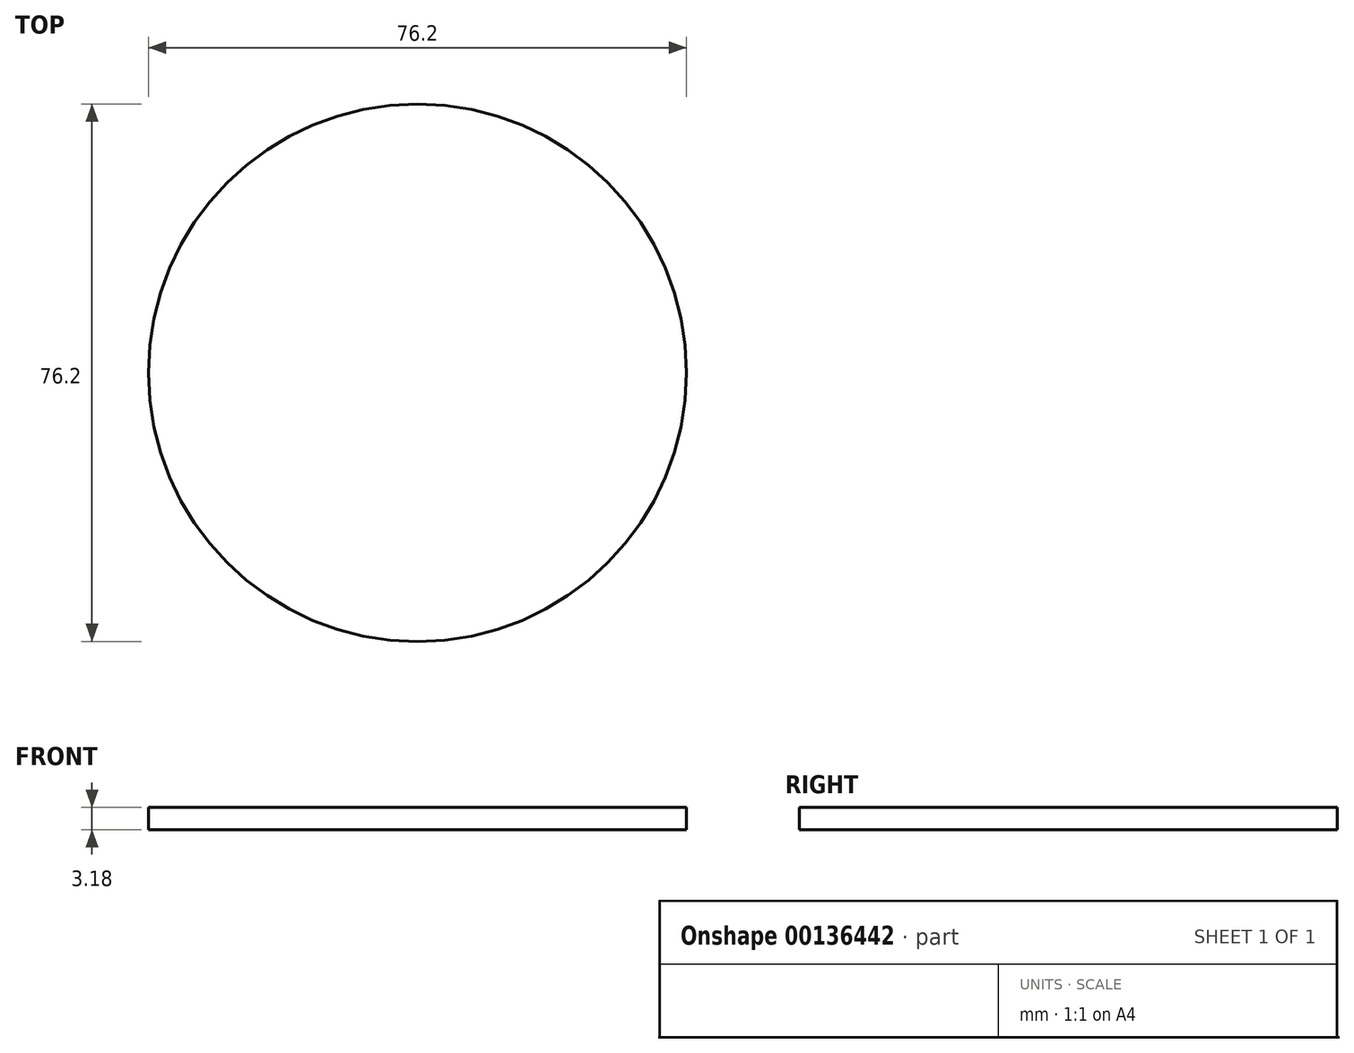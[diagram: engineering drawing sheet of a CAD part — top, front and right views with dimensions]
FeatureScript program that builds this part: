
annotation { "Feature Type Name" : "Feature", "Feature Type Description" : "" }
export const myFeature = defineFeature(function(context is Context, id is Id, definition is map)
    precondition{}
    {
        {
            var Q0;
            Q0=qCreatedBy(makeId("Top.planeOp"),FACE);
            var sketch = newSketch(context, id + "F0", { "sketchPlane" : qUnion([Q0])});
            skCircle(sketch, "E0", {"center": v(0, 1.61) * mm, "radius": 38.1 * mm});
            skSolve(sketch);
        }
        {
            var Q0;
            Q0=makeQuery(id+"F0.imprint","IMPRINT",FACE,{"disambiguationData":[TD([[makeQuery(id+"F0.imprint","IMPRINT",EDGE,{"derivedFrom":sQuery(id+"F0.wireOp",EDGE,"E0")}),1.0]])]});
            extrude(context, id + "F1", {"entities" : qUnion([Q0]), "depth" : 3.17 * mm});
        }
    });
